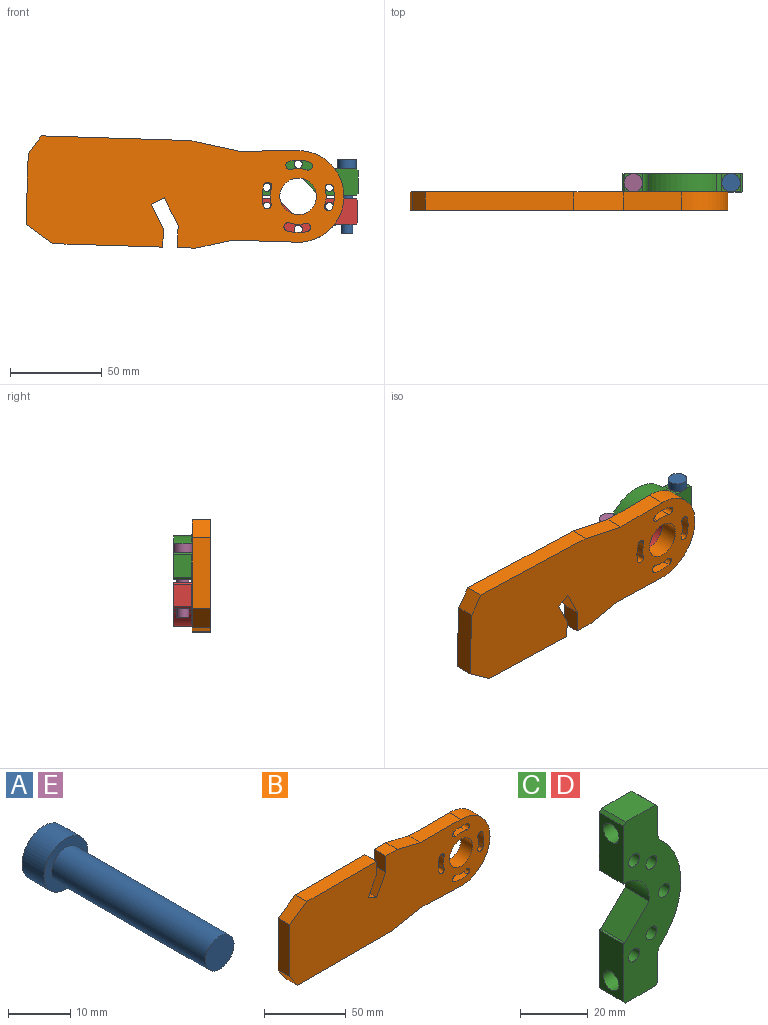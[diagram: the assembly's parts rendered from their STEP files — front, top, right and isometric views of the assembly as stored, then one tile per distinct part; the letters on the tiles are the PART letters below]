
ASSEMBLY  parts=5 mates=5
PART A: 5 faces, bbox 10x40x10 mm
  f0: cylinder r=3.25mm len=35mm, axis (0,1,0), area 714.7mm2, adj f1,f3
  f1: plane 6.5x6.5mm, normal (0,-1,0), area 33.2mm2, adj f0
  f2: cylinder r=5mm len=10mm, axis (0,1,0), area 157.1mm2, adj f3,f4
  f3: plane 10x10mm, normal (0,-1,0), area 45.4mm2, adj f0,f2
  f4: plane 10x10mm, normal (0,1,0), area 78.5mm2, adj f2
PART B: 35 faces, bbox 173x10x58.6 mm
  f0: plane 10x10mm, normal (0,0,1), area 100mm2, adj f1,f15,f16,f17
  f1: plane 12x10mm, normal (-1,0,0), area 120mm2, adj f0,f2,f16,f17
  f2: plane 15x10mm, normal (-0.88,0,0.47), area 170mm2, adj f1,f3,f16,f17
  f3: plane 10x7.06mm, normal (0.47,0,0.88), area 80mm2, adj f2,f4,f16,f17
  f4: plane 13.24x10mm, normal (0.88,0,-0.47), area 150mm2, adj f3,f5,f16,f17
  f5: plane 10x10mm, normal (1,0,0), area 100mm2, adj f4,f6,f16,f17
  f6: plane 60x10mm, normal (0,0,1), area 600mm2, adj f5,f7,f16,f17
  f7: plane 15x10mm, normal (-0.55,0,0.83), area 180.3mm2, adj f6,f8,f16,f17
  f8: plane 38.6x10mm, normal (-1,0,0), area 386mm2, adj f7,f9,f16,f17
  f9: plane 10x10mm, normal (-0.83,0,-0.56), area 121.1mm2, adj f8,f10,f16,f17
  f10: plane 81.17x10mm, normal (0,0,-1), area 811.7mm2, adj f9,f11,f16,f17
  f11: plane 27.1x10mm, normal (0.18,0,-0.98), area 275.6mm2, adj f10,f12,f16,f17
  f12: plane 31.82x10mm, normal (-0.04,0,-1), area 318.5mm2, adj f11,f13,f16,f17
  f13: cylinder r=25mm len=50mm, axis (0,1,0), area 796.2mm2, adj f12,f14,f16,f17
  f14: plane 35x10mm, normal (0,0,1), area 350mm2, adj f13,f15,f16,f17
  f15: plane 20x10mm, normal (0.24,0,0.97), area 206.2mm2, adj f0,f14,f16,f17
  f16: plane 173x58.6mm, normal (0,-1,0), area 8335.8mm2, adj f0,f1,f2,f3,f4,f5,f6,f7
  f17: plane 173x58.6mm, normal (0,1,0), area 8335.8mm2, adj f0,f1,f2,f3,f4,f5,f6,f7
  f18: cylinder r=2.25mm len=10mm, axis (0,-1,0), area 70.7mm2, adj f16,f17,f19,f21
  f19: cylinder r=19.75mm len=11.29mm, axis (0,-1,0), area 114.5mm2, adj f16,f17,f18,f20
  f20: cylinder r=2.25mm len=10mm, axis (0,-1,0), area 70.7mm2, adj f16,f17,f19,f21
  f21: cylinder r=15.25mm len=10mm, axis (0,-1,0), area 88.4mm2, adj f16,f17,f18,f20
  f22: cylinder r=2.25mm len=10mm, axis (0,-1,0), area 70.7mm2, adj f16,f17,f23,f25
  f23: cylinder r=15.25mm len=10mm, axis (0,-1,0), area 88.4mm2, adj f16,f17,f22,f24
  f24: cylinder r=2.25mm len=10mm, axis (0,-1,0), area 70.7mm2, adj f16,f17,f23,f25
  f25: cylinder r=19.75mm len=11.29mm, axis (0,-1,0), area 114.5mm2, adj f16,f17,f22,f24
  f26: cylinder r=2.25mm len=10mm, axis (0,-1,0), area 70.7mm2, adj f16,f17,f27,f29
  f27: cylinder r=15.25mm len=10mm, axis (0,-1,0), area 88.4mm2, adj f16,f17,f26,f28
  f28: cylinder r=2.25mm len=10mm, axis (0,-1,0), area 70.7mm2, adj f16,f17,f27,f29
  f29: cylinder r=19.75mm len=11.29mm, axis (0,-1,0), area 114.5mm2, adj f16,f17,f26,f28
  f30: cylinder r=2.25mm len=10mm, axis (0,-1,0), area 70.7mm2, adj f16,f17,f31,f33
  f31: cylinder r=19.75mm len=11.29mm, axis (0,-1,0), area 114.5mm2, adj f16,f17,f30,f32
  f32: cylinder r=2.25mm len=10mm, axis (0,-1,0), area 70.7mm2, adj f16,f17,f31,f33
  f33: cylinder r=15.25mm len=10mm, axis (0,-1,0), area 88.4mm2, adj f16,f17,f30,f32
  f34: cylinder r=10mm len=20mm, axis (0,-1,0), area 628.3mm2, adj f16,f17
PART C: 25 faces, bbox 24x10x65.3 mm
  f0: plane 20.86x10mm, normal (-1,0,0), area 175.4mm2, adj f1,f2,f3,f7,f21
  f1: plane 65.3x24mm, normal (0,1,0), area 966.5mm2, adj f0,f5,f6,f7,f8,f9,f10,f11
  f2: plane 65.3x24mm, normal (0,-1,0), area 966.5mm2, adj f0,f5,f6,f7,f8,f9,f10,f11
  f3: cylinder r=3.25mm len=14.46mm, axis (-1,0,0), area 295.2mm2, adj f0,f10
  f4: cylinder r=3.25mm len=14.46mm, axis (-1,0,0), area 295.2mm2, adj f14,f18
  f5: cylinder r=2.25mm len=10mm, axis (0,1,0), area 141.4mm2, adj f1,f2
  f6: cylinder r=2.25mm len=10mm, axis (0,1,0), area 141.4mm2, adj f1,f2
  f7: plane 10x1mm, normal (-0.71,0,-0.71), area 14.1mm2, adj f0,f1,f2,f8
  f8: plane 12.46x10mm, normal (0,0,-1), area 124.5mm2, adj f1,f2,f7,f9
  f9: plane 10x1mm, normal (0.71,0,-0.71), area 14.1mm2, adj f1,f2,f8,f10
  f10: plane 10.14x10mm, normal (1,0,0), area 68.3mm2, adj f1,f2,f3,f9,f11
  f11: cylinder r=4mm len=10mm, axis (0,1,0), area 33.4mm2, adj f1,f2,f10,f12
  f12: cylinder r=25mm len=37.08mm, axis (0,-1,0), area 417.7mm2, adj f1,f2,f11,f13
  f13: cylinder r=4mm len=10mm, axis (0,1,0), area 33.4mm2, adj f1,f2,f12,f14
  f14: plane 10.14x10mm, normal (1,0,0), area 68.3mm2, adj f1,f2,f4,f13,f15
  f15: plane 10x1mm, normal (0.71,0,0.71), area 14.1mm2, adj f1,f2,f14,f16
  f16: plane 12.46x10mm, normal (0,0,1), area 124.5mm2, adj f1,f2,f15,f17
  f17: plane 10x1mm, normal (-0.71,0,0.71), area 14.1mm2, adj f1,f2,f16,f18
  f18: plane 20.86x10mm, normal (-1,0,0), area 175.4mm2, adj f1,f2,f4,f17,f20
  f19: plane 10.04x10.04mm, normal (-0.71,0,0.71), area 142mm2, adj f1,f2,f20,f21
  f20: cylinder r=10.46mm len=11.51mm, axis (0,1,0), area 178.2mm2, adj f1,f2,f18,f19
  f21: cylinder r=10.46mm len=10mm, axis (0,1,0), area 7.1mm2, adj f0,f1,f2,f19
  f22: cylinder r=2.25mm len=10mm, axis (0,1,0), area 141.4mm2, adj f1,f2
  f23: cylinder r=2.25mm len=10mm, axis (0,1,0), area 141.4mm2, adj f1,f2
  f24: cylinder r=2.25mm len=10mm, axis (0,1,0), area 141.4mm2, adj f1,f2
PART D: same geometry as C
PART E: same geometry as A
PLACE A rot(axis=(1,0,0),90deg) t=(99.47,83.08,24.74)mm
PLACE B rot(axis=(1,0,-0.02),180deg) t=(21.94,14.49,-9)mm
PLACE C rot(axis=(0,-1,0),90deg) t=(17.44,24.49,-4.81)mm fixed
PLACE D rot(axis=(0,1,0),90deg) t=(45.52,24.49,13.84)mm fixed
PLACE E rot(axis=(1,0,0),90deg) t=(46.16,83.08,24.74)mm
MATE revolute B.f13 <-> D.f12  axis (0,1,0) through (31.48,24.49,4.74)mm
MATE cylindrical D.f4 <-> A.f0  axis (0,0,1) through (58.13,29.49,3.74)mm
MATE cylindrical E.f0 <-> D.f3  axis (0,0,1) through (4.83,29.49,2.24)mm
MATE fastened E.f0 <-> C.f4  axis (0,0,-1) through (4.83,29.49,19.74)mm
MATE fastened A.f0 <-> C.f3  axis (0,0,-1) through (58.13,29.49,19.74)mm
